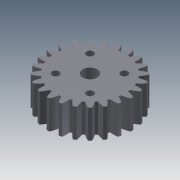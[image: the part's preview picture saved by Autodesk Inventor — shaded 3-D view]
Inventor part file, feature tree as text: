
AUTODESK INVENTOR PART (.ipt)
format: ipt  version: 2015 (Build 190159000, 159)  size: 376,320 bytes
history: native  units: mm (DEFAULTED — no unit token found)
features: other x8, sketch x4, plane x3, extrude x2, projected_geometry x1
ambient origin geometry x8: Origin, YZ Plane, XZ Plane, XY Plane, X Axis, Y Axis, Z Axis, Center Point
bodies: Solid1 (feature_tree)
feature tree (18):
  other  "Blocks"
  extrude  "Extrusion1"  Depth=20.0mm TaperAngle=0.0deg
  plane  "Work Plane2"
  plane  "Work Plane8"
  plane  "Work Plane9"
  other  "Spur Gear"
  extrude  "Extrusion3"  Depth=10.0mm TaperAngle=0.0deg
  sketch  "Sketch4"  dims[d17=0.0mm d34=1.308997mm d39=0.0mm d41=0.0mm d43=70.0mm d46=70.0mm d47=0.0mm d48=0.0mm d49=10.0mm d52=5.0mm d53=12.0mm d54=12.0mm d55=10.0mm d56=0.0mm]
  other  "DXF"
  sketch  "Sketch1"  dims[d0=58.493319mm d1=20.0mm d2=0.0mm]
  sketch  "Sketch2"  dims[d3=54.193548mm d4=10.0mm d5=0.0mm]
  other  "Srf1"
  sketch  "Sketch3"  dims[d16=70.0mm]
  projected_geometry  "Projected Loop1"
  other  "Block1"
  other  "Pitch Diameter"
  other  "Block1:1"
  other  "Block1:2"
